# Revit family: Time Max F
name_source: partatom
category: Attrezzatura meccanica
units: mm (PartAtom-declared; Revit-internal decimal feet)

## family parameters
Basato su piano di lavoro = No
Classificazione = Nessuno
Condiviso = No
Mantieni orientamento annotazione = No
Punto di calcolo locali = No
Quota connettore circolare = Usa diametro
Sempre verticale = Sì
Taglio con vuoti quando caricato = No
Tipo di parte = Normale

## types (2) — shared parameters
Date of publishing = 18/03/2024
Depth = 425 mm  [stored 1.39436 ft]
Design country = Italy
Domestic Cold Water Diameter = 21 mm  [stored 0.0688976 ft]
Domestic Hot Water Diameter = 21 mm  [stored 0.0688976 ft]
Flue outlet = 80 mm  [stored 0.262467 ft]
Gas Inlet Diameter = 26 mm
Height = 900 mm  [stored 2.95276 ft]
Hydronic Return Diameter = 26 mm
Hydronic Supply Diameter = 26 mm
IFC Classification = Boilers
Manufacturer country = Italy
Manufacturer name = Italtherm S.p.A.
Material main = Metal
Material secondary = Plastic
Max supply pressure = 8 bar
Max system temperature = 83°C
Max working pressure = 3 bar
NBS reference Description = Boilers
Power supply | Frequency (Hz) = 50 Hz
Power supply | Phase = 1
Power supply | Voltage (V) = 230 V
Product family = Heating
Product group = Thermal unit
Uniclass 2015 Name = Boilers
Width = 600 mm  [stored 1.9685 ft]
zero-valued in all types: Prospetto di default

## per-type parameters (varying)
| type | Efficiency 30% | Max heat input (Qn) | Max heat output (Pn) | Min heat input (Qr) | Min heat output (Pr) | Power consumption (W) | Weight |
| Time Max 24 F | 91,70% | 25.7 kW | 23.8 kW | 10.3 kW | 9.1 kW | 130 W | 60,00 kg |
| Time Max 30 F | 90,60% | 32 kW | 29.9 kW | 13 kW | 11.2 kW | 140 W | 60,50 kg |

note: [stored X ft] marks values corroborated as IEEE doubles in the binary element streams (Revit-internal decimal feet)
